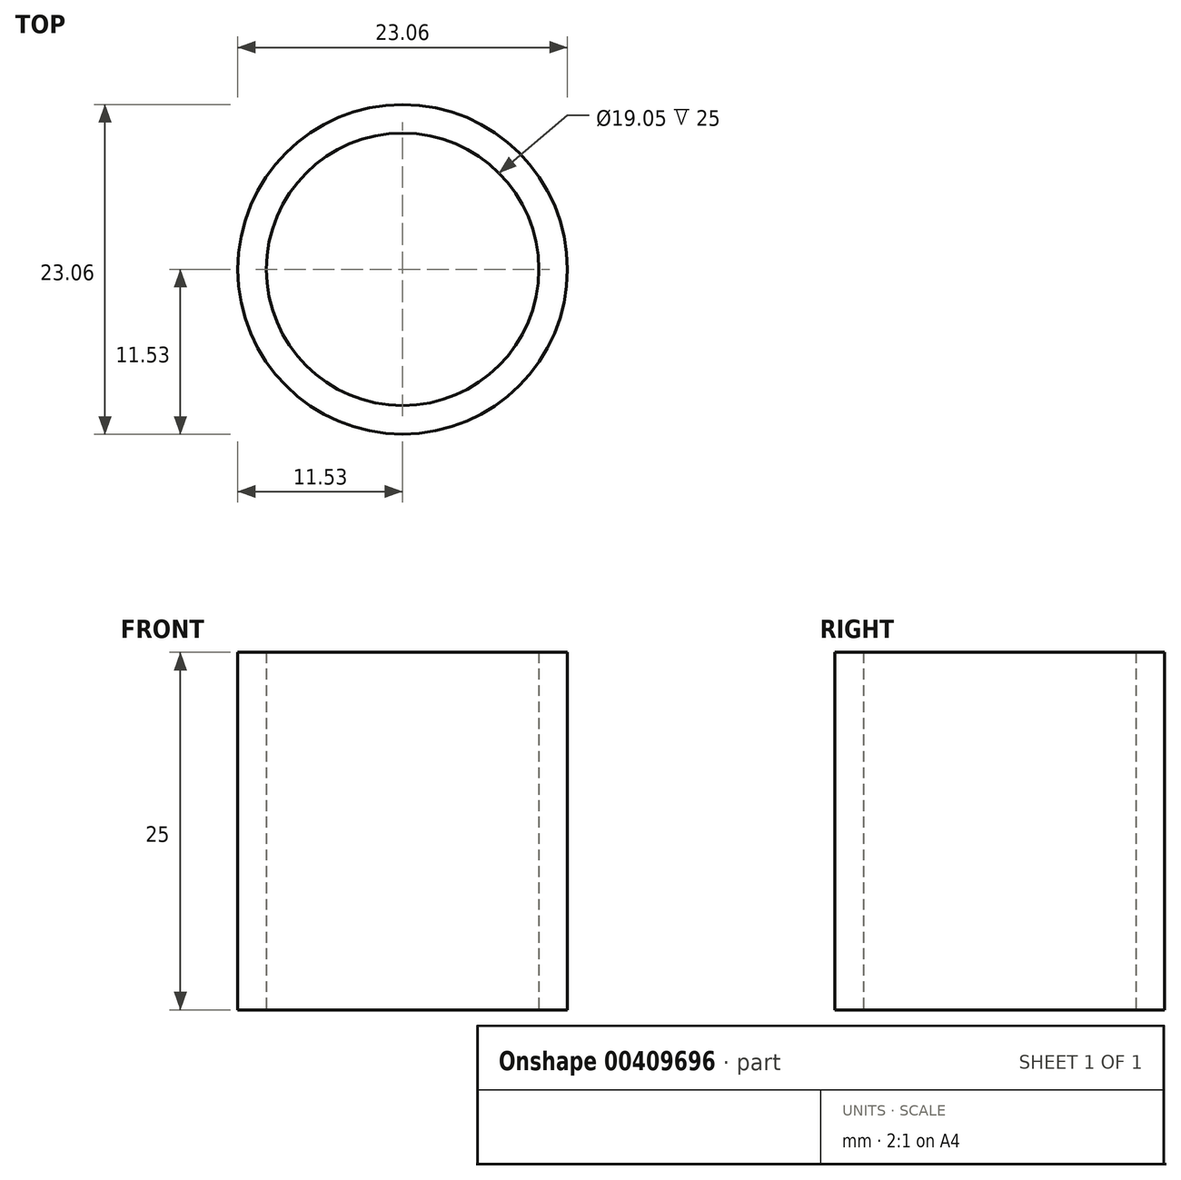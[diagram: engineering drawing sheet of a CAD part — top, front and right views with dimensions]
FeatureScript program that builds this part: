
annotation { "Feature Type Name" : "Feature", "Feature Type Description" : "" }
export const myFeature = defineFeature(function(context is Context, id is Id, definition is map)
    precondition{}
    {
        {
            var Q0;
            Q0=qCreatedBy(makeId("Top.planeOp"),FACE);
            var sketch = newSketch(context, id + "F0", { "sketchPlane" : qUnion([Q0])});
            skCircle(sketch, "E0", {"center": v(0, 0) * mm, "radius": 11.53 * mm});
            skCircle(sketch, "E1", {"center": v(0, 0) * mm, "radius": 9.53 * mm});
            skLineSegment(sketch, "E2", {"start": v(9.53, 0) * mm, "end": v(11.53, 0) * mm, "construction": true});
            skSolve(sketch);
        }
        {
            var Q0;
            Q0=makeQuery(id+"F0.imprint","IMPRINT",FACE,{"disambiguationData":[TD([[makeQuery(id+"F0.imprint","IMPRINT",EDGE,{"derivedFrom":sQuery(id+"F0.wireOp",EDGE,"E0")}),1.0]])]});
            extrude(context, id + "F1", {"entities" : qUnion([Q0]), "depth" : 25 * mm});
        }
    });
